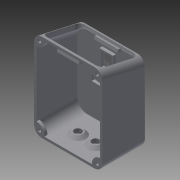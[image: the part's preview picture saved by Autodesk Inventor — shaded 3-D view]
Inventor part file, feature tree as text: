
AUTODESK INVENTOR PART (.ipt)
format: ipt  version: 2014 (Build 180170000, 170)  size: 431,616 bytes
history: native  units: mm
features: sketch x15, extrude x11, fillet x6, chamfer x3, loft x2, plane x1, projected_geometry x1
ambient origin geometry x8: Origin, YZ Plane, XZ Plane, XY Plane, X Axis, Y Axis, Z Axis, Center Point
bodies: Solid1 (feature_tree)
feature tree (39):
  sketch  "Sketch1"  dims[d0=70.0mm d1=90.0mm]
  plane  "Work Plane1"
  loft  "Loft1"
  sketch  "Sketch3"  dims[d6=0.0mm d7=90.0deg d8=60.0mm]
  sketch  "Sketch4"  dims[d9=40.0mm d10=65.0mm d11=85.0mm d12=65.0mm]
  sketch  "Sketch5"  dims[d13=75.0mm d14=5.0mm d15=0.0mm d16=5.0mm]
  extrude  "Extrusion1"  Depth=80.0mm
  fillet  "Fillet1"  [1 undecoded]
  loft  "Loft2"
  extrude  "Extrusion2"  Depth=65.0mm
  fillet  "Fillet2"  Radius=85.0mm
  fillet  "Fillet3"  Radius=65.0mm
  extrude  "Extrusion3"  Depth=75.0mm TaperAngle=0.0deg
  fillet  "Fillet4"  Radius=5.0mm
  extrude  "Extrusion4"  TaperAngle=0.0deg  [1 undecoded]
  extrude  "Extrusion5"  Depth=8.0mm
  extrude  "Extrusion6"  Depth=3.0mm TaperAngle=0.0deg
  chamfer  "Chamfer1"  Distance=3.0mm
  fillet  "Fillet5"  Radius=11.0mm
  extrude  "Extrusion7"  Depth=11.0mm
  extrude  "Extrusion8"  Depth=15.0mm
  chamfer  "Chamfer2"  Distance=3.0mm
  extrude  "Extrusion10"  Depth=3.0mm TaperAngle=0.0deg
  extrude  "Extrusion11"  Depth=15.0mm
  fillet  "Fillet6"  Radius=3.0mm
  extrude  "Extrusion12"  Depth=3.0mm
  chamfer  "Chamfer3"  Distance=18.0mm
  sketch  "Sketch2"  dims[d2=45.0mm d3=80.0mm d4=0.0mm d5=90.0deg]
  sketch  "Sketch6"  dims[d17=0.0mm d18=90.0deg d19=0.0mm d20=90.0deg]
  sketch  "Sketch7"  dims[d21=3.0mm d22=0.0mm d23=8.0mm]
  projected_geometry  "Projected Loop1"
  sketch  "Sketch8"  dims[d24=10.0mm d25=3.0mm d26=0.0mm]
  sketch  "Sketch9"  dims[d27=2.0mm]
  sketch  "Sketch10"  dims[d28=9.5mm d29=3.0mm d30=0.0mm d31=11.0mm]
  sketch  "Sketch11"  dims[d32=6.0mm d33=11.0mm]
  sketch  "Sketch12"  dims[d34=6.0mm d35=15.0mm]
  sketch  "Sketch14"  dims[d36=15.0mm]
  sketch  "Sketch15"  dims[d37=37.280029mm d38=3.0mm d39=0.0mm]
  sketch  "Sketch16"  dims[d40=10.0mm d41=3.0mm d42=0.0mm d43=15.0mm d44=3.0mm d45=2.0mm d46=45.0deg d47=3.0mm d48=18.0mm d49=18.0mm d50=18.0mm d51=18.0mm d52=3.0mm d53=0.0mm d54=2.5mm d55=2.5mm d56=2.5mm d57=2.5mm d58=3.0mm d59=0.0mm d60=0.5mm d61=2.0mm d62=45.0deg d69=11.0mm d70=13.0mm d71=2.0mm d72=1.5mm d73=1.5mm d74=1.5mm d75=1.5mm d76=3.0mm d77=0.0mm d78=7.5mm d79=7.5mm d80=19.0mm d81=19.0mm d82=18.0mm d83=18.0mm d84=3.0mm d85=0.0mm d86=2.0mm d87=10.0mm d88=10.0mm d89=3.0mm d90=0.0mm d91=3.0mm d92=2.0mm d93=45.0deg]
note: 2 required parameter values undecoded (feature->parameter linkage not recoverable at this tier; creation-order binding heuristic only, values carry confidence <= 0.55)
